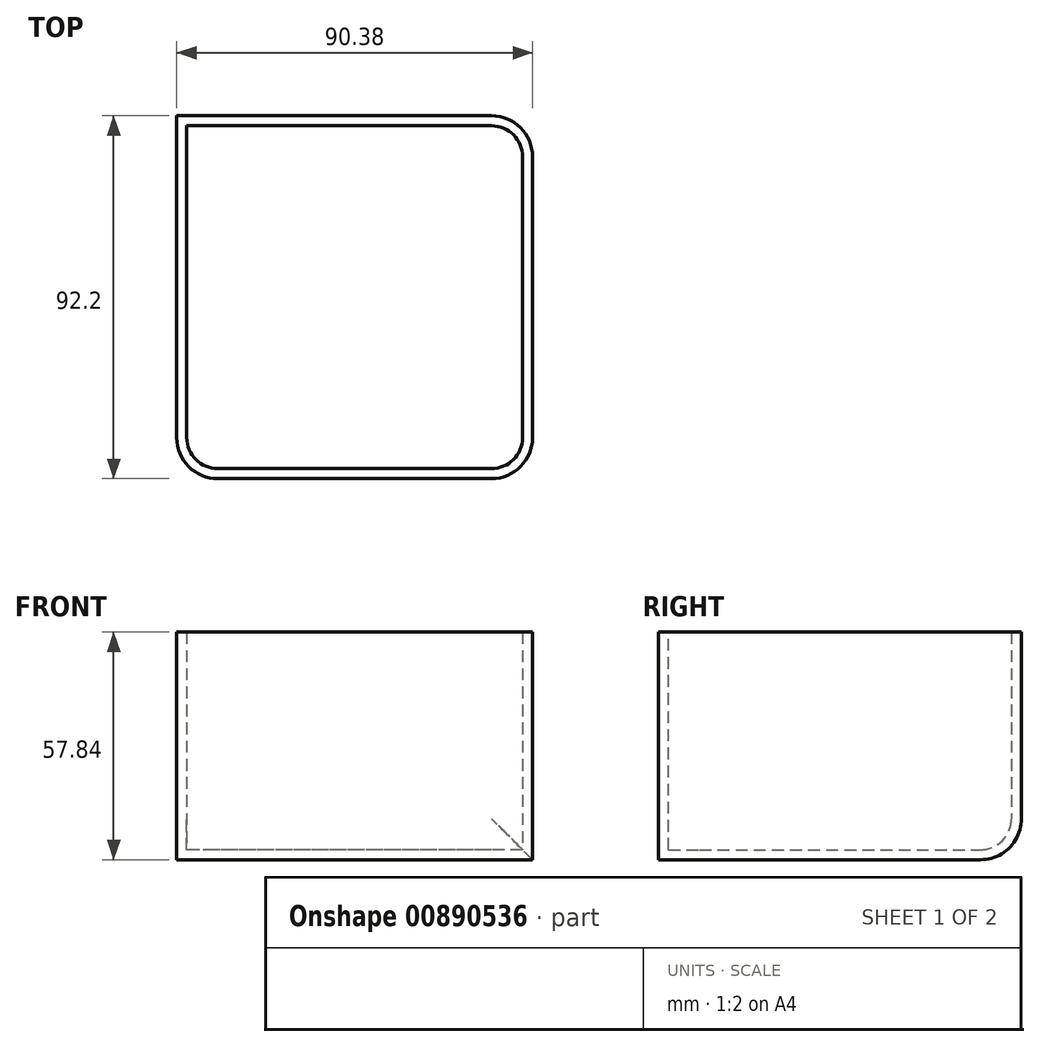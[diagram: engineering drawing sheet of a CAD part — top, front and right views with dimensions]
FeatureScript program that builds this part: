
annotation { "Feature Type Name" : "Feature", "Feature Type Description" : "" }
export const myFeature = defineFeature(function(context is Context, id is Id, definition is map)
    precondition{}
    {
        {
            var Q0;
            Q0=qCreatedBy(makeId("Front.planeOp"),FACE);
            var sketch = newSketch(context, id + "F0", { "sketchPlane" : qUnion([Q0])});
            skLineSegment(sketch, "E0.bottom", {"start": v(45.19, 28.92) * mm, "end": v(-45.19, 28.92) * mm});
            skLineSegment(sketch, "E0.top", {"start": v(45.19, -28.92) * mm, "end": v(-45.19, -28.92) * mm});
            skLineSegment(sketch, "E0.left", {"start": v(45.19, 28.92) * mm, "end": v(45.19, -28.92) * mm});
            skLineSegment(sketch, "E0.right", {"start": v(-45.19, 28.92) * mm, "end": v(-45.19, -28.92) * mm});
            skPoint(sketch, "E0.middle", {"position": v(0, 0) * mm});
            skSolve(sketch);
        }
        {
            var Q0;
            Q0=makeQuery(id+"F0.imprint","IMPRINT",FACE,{"disambiguationData":[TD([[makeQuery(id+"F0.imprint","IMPRINT",EDGE,{"derivedFrom":sQuery(id+"F0.wireOp",EDGE,"E0.bottom")}),1.0]])]});
            extrude(context, id + "F1", {"entities" : qUnion([Q0]), "depth" : 92.2 * mm, "offsetDistance" : 25.4 * mm});
        }
        {
            var Q0;
            Q0=makeQuery(id+"F1.opExtrude","CAP_EDGE",EDGE,{"disambiguationData":[OSD([sQuery(id+"F0.wireOp",EDGE,"E0.left")])],"isStart":false});
            var Q1;
            Q1=makeQuery(id+"F1.opExtrude","CAP_EDGE",EDGE,{"disambiguationData":[OSD([sQuery(id+"F0.wireOp",EDGE,"E0.right")])],"isStart":false});
            var Q2;
            Q2=makeQuery(id+"F1.opExtrude","CAP_EDGE",EDGE,{"disambiguationData":[OSD([sQuery(id+"F0.wireOp",EDGE,"E0.left")])],"isStart":true});
            var Q3;
            Q3=makeQuery(id+"F1.opExtrude","CAP_EDGE",EDGE,{"disambiguationData":[OSD([sQuery(id+"F0.wireOp",EDGE,"E0.top")])],"isStart":true});
            fillet(context, id + "F2", {"entities" : qUnion([Q0, Q1, Q2, Q3]), "radius" : 10.42 * mm, "tangentPropagation" : true, "allowEdgeOverflow" : false});
        }
        {
            var Q0;
            Q0=makeQuery(id+"F1.opExtrude","SWEPT_FACE",FACE,{"disambiguationData":[OSD([sQuery(id+"F0.wireOp",EDGE,"E0.bottom")])]});
            shell(context, id + "F3", {"entities" : qUnion([Q0]), "thickness" : 2.54 * mm});
        }
    });
